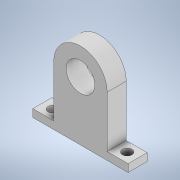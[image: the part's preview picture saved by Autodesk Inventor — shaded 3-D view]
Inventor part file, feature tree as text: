
AUTODESK INVENTOR PART (.ipt)
format: ipt  version: 2021 (Build 250183000, 183)  size: 124,928 bytes
history: native  units: mm
features: extrude x2, sketch x2, other x1
ambient origin geometry x8: Origin, YZ Plane, XZ Plane, XY Plane, X Axis, Y Axis, Z Axis, Center Point
bodies: Body1 (feature_tree)
feature tree (5):
  other  "Sólido1"
  extrude  "Extrusión1"  Depth=7.5mm
  extrude  "Extrusión2"  Depth=28.0mm TaperAngle=0.0deg
  sketch  "Boceto1"  dims[d0=10.0mm d1=0.0mm d2=7.5mm]
  sketch  "Boceto2"  dims[d3=5.0mm d4=5.0mm d5=0.0mm d6=50.0mm d7=28.0mm d8=0.375mm d9=14.3117mm d10=0.75mm d11=20.594885mm d12=0.0625mm d13=0.75mm d14=0.375mm]
